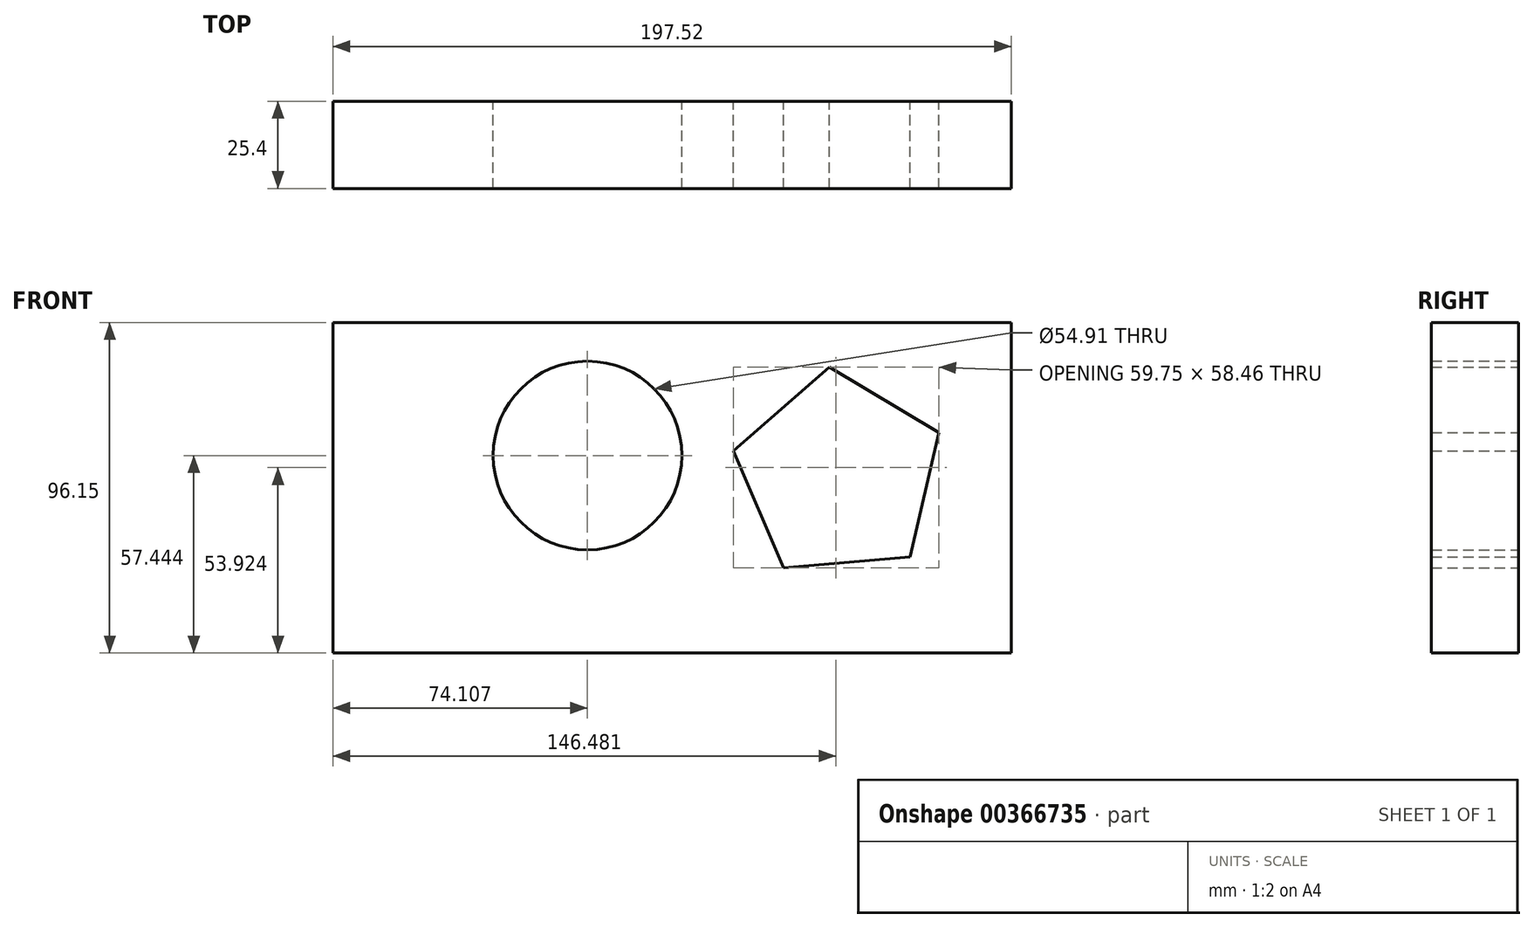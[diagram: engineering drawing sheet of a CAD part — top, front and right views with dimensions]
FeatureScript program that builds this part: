
annotation { "Feature Type Name" : "Feature", "Feature Type Description" : "" }
export const myFeature = defineFeature(function(context is Context, id is Id, definition is map)
    precondition{}
    {
        {
            var Q0;
            Q0=qCreatedBy(makeId("Front.planeOp"),FACE);
            var sketch = newSketch(context, id + "F0", { "sketchPlane" : qUnion([Q0])});
            skLineSegment(sketch, "E0.bottom", {"start": v(-63.02, 58.1) * mm, "end": v(134.5, 58.1) * mm});
            skLineSegment(sketch, "E0.top", {"start": v(-63.02, -38.05) * mm, "end": v(134.5, -38.05) * mm});
            skLineSegment(sketch, "E0.left", {"start": v(-63.02, 58.1) * mm, "end": v(-63.02, -38.05) * mm});
            skLineSegment(sketch, "E0.right", {"start": v(134.5, 58.1) * mm, "end": v(134.5, -38.05) * mm});
            skCircle(sketch, "E1", {"center": v(11.09, 19.4) * mm, "radius": 27.45 * mm});
            skCircle(sketch, "E2.cCircle", {"center": v(84.32, 13.7) * mm, "radius": 31.54 * mm, "construction": true});
            skLineSegment(sketch, "E2.0", {"start": v(105.04, -10.09) * mm, "end": v(68.1, -13.36) * mm});
            skLineSegment(sketch, "E2.1", {"start": v(68.1, -13.36) * mm, "end": v(53.58, 20.75) * mm});
            skLineSegment(sketch, "E2.2", {"start": v(53.58, 20.75) * mm, "end": v(81.54, 45.1) * mm});
            skLineSegment(sketch, "E2.3", {"start": v(81.54, 45.1) * mm, "end": v(113.34, 26.04) * mm});
            skLineSegment(sketch, "E2.4", {"start": v(113.34, 26.04) * mm, "end": v(105.04, -10.09) * mm});
            skSolve(sketch);
        }
        {
            var Q0;
            Q0=makeQuery(id+"F0.imprint","IMPRINT",FACE,{"disambiguationData":[TD([[makeQuery(id+"F0.imprint","IMPRINT",EDGE,{"derivedFrom":sQuery(id+"F0.wireOp",EDGE,"E0.bottom")}),-1.0]])]});
            extrude(context, id + "F1", {"entities" : qUnion([Q0]), "depth" : 25.4 * mm});
        }
    });
